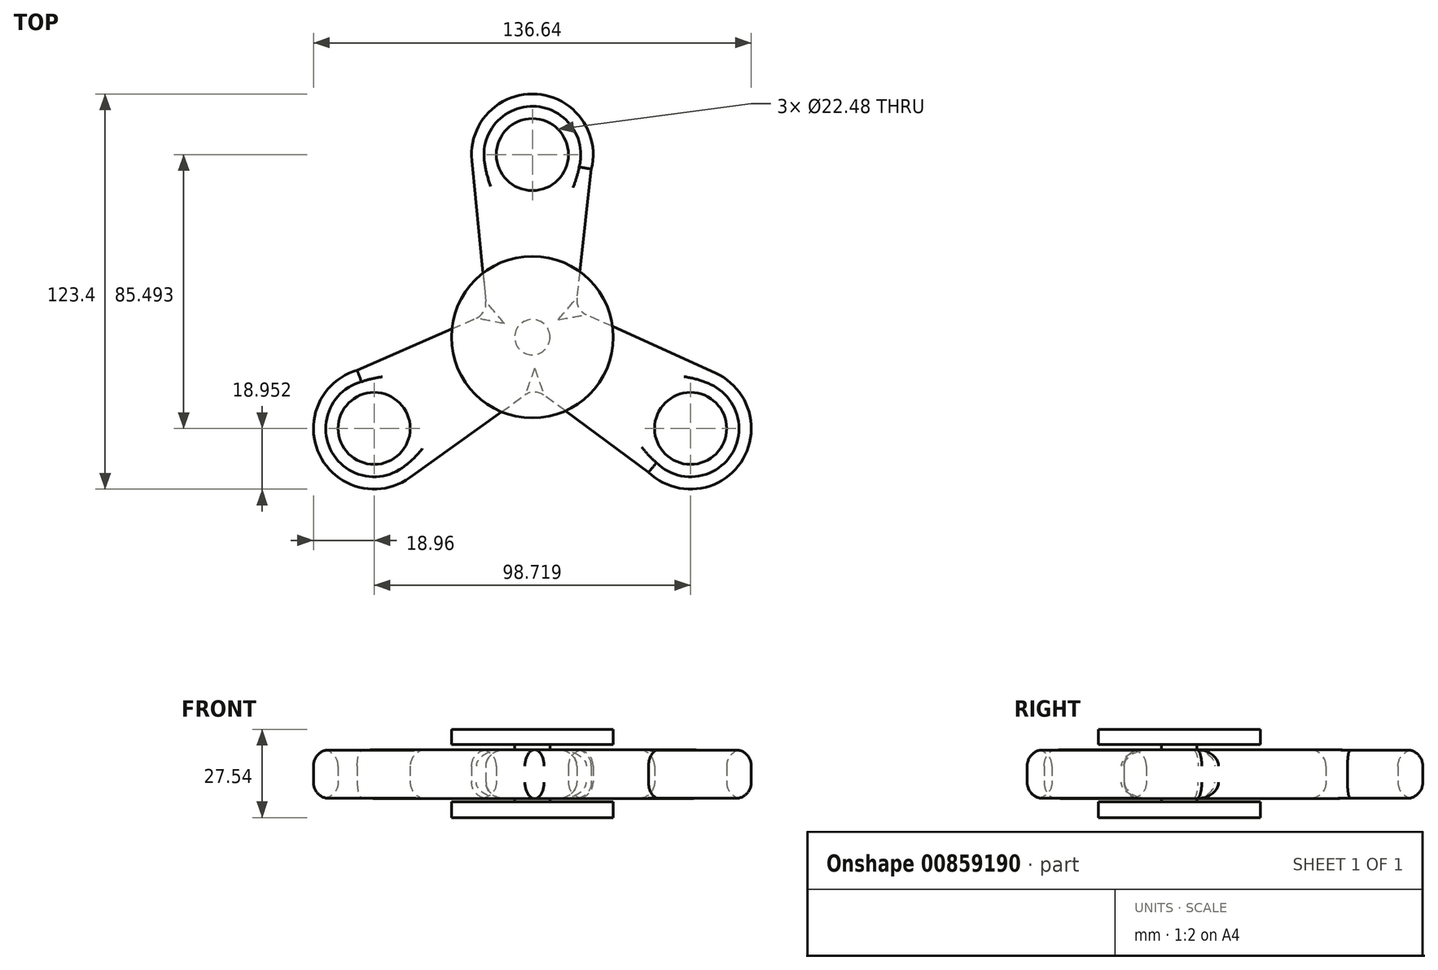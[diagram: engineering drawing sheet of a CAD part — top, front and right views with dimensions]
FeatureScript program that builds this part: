
annotation { "Feature Type Name" : "Feature", "Feature Type Description" : "" }
export const myFeature = defineFeature(function(context is Context, id is Id, definition is map)
    precondition{}
    {
        {
            var Q0;
            Q0=qCreatedBy(makeId("Top.planeOp"),FACE);
            var sketch = newSketch(context, id + "F0", { "sketchPlane" : qUnion([Q0])});
            skArc(sketch, "E0", {"start": v(18.4, 52.47) * mm, "mid": v(1.35, 75.9) * mm, "end": v(-18.86, 55.13) * mm});
            skCircle(sketch, "E1", {"center": v(0, 57) * mm, "radius": 11.24 * mm});
            skLineSegment(sketch, "E2", {"start": v(-18.86, 55.13) * mm, "end": v(-13.4, 0) * mm});
            skLineSegment(sketch, "E3", {"start": v(18.95, 57.32) * mm, "end": v(12.51, 0) * mm});
            skLineSegment(sketch, "E4", {"start": v(12.51, 0) * mm, "end": v(-13.4, 0) * mm});
            skSolve(sketch);
        }
        {
            var Q0;
            Q0 = qSketchRegion(id + "F0", true);
            extrude(context, id + "F1", {"entities" : qUnion([Q0]), "endBound" : BoundingType.SYMMETRIC, "depth" : 15.24 * mm, "offsetDistance" : 25.4 * mm});
        }
        {
            var Q0;
            Q0=qCreatedBy(makeId("Top.planeOp"),FACE);
            var sketch = newSketch(context, id + "F2", { "sketchPlane" : qUnion([Q0])});
            skCircle(sketch, "E5", {"center": v(0, 0) * mm, "radius": 28.62 * mm});
            skSolve(sketch);
        }
        {
            var Q0;
            Q0=makeQuery(id+"F1.opExtrude","SWEPT_BODY",BODY,{"disambiguationData":[OSD([sQuery(id+"F0.wireOp",EDGE,"E0"),sQuery(id+"F0.wireOp",EDGE,"E1"),sQuery(id+"F0.wireOp",EDGE,"E2"),sQuery(id+"F0.wireOp",EDGE,"E3"),sQuery(id+"F0.wireOp",EDGE,"E4")])]});
            var Q1;
            Q1=sQuery(id+"F2.wireOp",EDGE,"E5");
            circularPattern(context, id + "F3", {"operationType" : NewBodyOperationType.ADD, "entities" : qUnion([Q0]), "axis" : qUnion([Q1]), "angle" : 360 * degree, "instanceCount" : 3, "equalSpace" : true});
        }
        {
            var Q0;
            {var subQ0=makeQuery(id+"F1.opExtrude","CAP_FACE",FACE,{"disambiguationData":[OSD([sQuery(id+"F0.wireOp",EDGE,"E0"),sQuery(id+"F0.wireOp",EDGE,"E1"),sQuery(id+"F0.wireOp",EDGE,"E2"),sQuery(id+"F0.wireOp",EDGE,"E3"),sQuery(id+"F0.wireOp",EDGE,"E4")])],"isStart":false});Q0=makeQuery(id+"F3.boolean.opBoolean","MERGE",FACE,{"derivedFrom":[subQ0,makeQuery(id+"F3.opPattern","COPY",FACE,{"derivedFrom":subQ0,"instanceName":"1"}),makeQuery(id+"F3.opPattern","COPY",FACE,{"derivedFrom":subQ0,"instanceName":"2"})]});}
            var Q1;
            Q1=makeQuery(id+"F3.opPattern","COPY",EDGE,{"derivedFrom":makeQuery(id+"F1.opExtrude","CAP_EDGE",EDGE,{"disambiguationData":[OSD([sQuery(id+"F0.wireOp",EDGE,"E3")])],"isStart":true}),"instanceName":"1"});
            var Q2;
            {var subQ0=makeQuery(id+"F1.opExtrude","CAP_FACE",FACE,{"disambiguationData":[OSD([sQuery(id+"F0.wireOp",EDGE,"E0"),sQuery(id+"F0.wireOp",EDGE,"E1"),sQuery(id+"F0.wireOp",EDGE,"E2"),sQuery(id+"F0.wireOp",EDGE,"E3"),sQuery(id+"F0.wireOp",EDGE,"E4")])],"isStart":true});Q2=makeQuery(id+"F3.boolean.opBoolean","MERGE",FACE,{"derivedFrom":[subQ0,makeQuery(id+"F3.opPattern","COPY",FACE,{"derivedFrom":subQ0,"instanceName":"1"}),makeQuery(id+"F3.opPattern","COPY",FACE,{"derivedFrom":subQ0,"instanceName":"2"})]});}
            fillet(context, id + "F4", {"entities" : qUnion([Q0, Q1, Q2]), "radius" : 5.08 * mm, "tangentPropagation" : true, "allowEdgeOverflow" : false});
        }
        {
            var Q0;
            Q0=makeQuery(id+"F3.boolean.opBoolean","INTERSECT",EDGE,{"derivedFrom":[makeQuery(id+"F1.opExtrude","SWEPT_FACE",FACE,{"disambiguationData":[OSD([sQuery(id+"F0.wireOp",EDGE,"E2")])]}),makeQuery(id+"F3.opPattern","COPY",FACE,{"derivedFrom":makeQuery(id+"F1.opExtrude","SWEPT_FACE",FACE,{"disambiguationData":[OSD([sQuery(id+"F0.wireOp",EDGE,"E3")])]}),"instanceName":"1"})]});
            var Q1;
            Q1=makeQuery(id+"F3.boolean.opBoolean","INTERSECT",EDGE,{"derivedFrom":[makeQuery(id+"F1.opExtrude","SWEPT_FACE",FACE,{"disambiguationData":[OSD([sQuery(id+"F0.wireOp",EDGE,"E3")])]}),makeQuery(id+"F3.opPattern","COPY",FACE,{"derivedFrom":makeQuery(id+"F1.opExtrude","SWEPT_FACE",FACE,{"disambiguationData":[OSD([sQuery(id+"F0.wireOp",EDGE,"E2")])]}),"instanceName":"2"})]});
            var Q2;
            Q2=makeQuery(id+"F3.boolean.opBoolean","INTERSECT",EDGE,{"derivedFrom":[makeQuery(id+"F3.opPattern","COPY",FACE,{"derivedFrom":makeQuery(id+"F1.opExtrude","SWEPT_FACE",FACE,{"disambiguationData":[OSD([sQuery(id+"F0.wireOp",EDGE,"E2")])]}),"instanceName":"1"}),makeQuery(id+"F3.opPattern","COPY",FACE,{"derivedFrom":makeQuery(id+"F1.opExtrude","SWEPT_FACE",FACE,{"disambiguationData":[OSD([sQuery(id+"F0.wireOp",EDGE,"E3")])]}),"instanceName":"2"})]});
            fillet(context, id + "F5", {"entities" : qUnion([Q0, Q1, Q2]), "radius" : 5.08 * mm, "tangentPropagation" : true, "allowEdgeOverflow" : false});
        }
        {
            var Q0;
            Q0=qCreatedBy(makeId("Top.planeOp"),FACE);
            var sketch = newSketch(context, id + "F6", { "sketchPlane" : qUnion([Q0])});
            skCircle(sketch, "E6", {"center": v(0, 0) * mm, "radius": 5.51 * mm});
            skSolve(sketch);
        }
        {
            var Q0;
            Q0 = qSketchRegion(id + "F6", true);
            extrude(context, id + "F7", {"entities" : qUnion([Q0]), "operationType" : NewBodyOperationType.ADD, "endBound" : BoundingType.SYMMETRIC, "depth" : 19.3 * mm, "offsetDistance" : 25.4 * mm});
        }
        {
            var Q0;
            Q0=qCreatedBy(makeId("Front.planeOp"),FACE);
            var sketch = newSketch(context, id + "F8", { "sketchPlane" : qUnion([Q0])});
            skLineSegment(sketch, "E7.bottom", {"start": v(0, 14) * mm, "end": v(-25.25, 14) * mm});
            skLineSegment(sketch, "E7.top", {"start": v(0, 9.28) * mm, "end": v(-25.25, 9.28) * mm});
            skLineSegment(sketch, "E7.left", {"start": v(0, 14) * mm, "end": v(0, 9.28) * mm});
            skLineSegment(sketch, "E7.right", {"start": v(-25.25, 14) * mm, "end": v(-25.25, 9.28) * mm});
            skLineSegment(sketch, "E8.bottom", {"start": v(0, -8.66) * mm, "end": v(-25.25, -8.66) * mm});
            skLineSegment(sketch, "E8.top", {"start": v(0, -13.55) * mm, "end": v(-25.25, -13.55) * mm});
            skLineSegment(sketch, "E8.left", {"start": v(0, -8.66) * mm, "end": v(0, -13.55) * mm});
            skLineSegment(sketch, "E8.right", {"start": v(-25.25, -8.66) * mm, "end": v(-25.25, -13.55) * mm});
            skSolve(sketch);
        }
        {
            var Q0;
            Q0 = qSketchRegion(id + "F8", true);
            var Q1;
            Q1=sQuery(id+"F8.wireOp",EDGE,"E8.left");
            revolve(context, id + "F9", {"operationType" : NewBodyOperationType.ADD, "surfaceOperationType" : NewSurfaceOperationType.NEW, "entities" : qUnion([Q0]), "axis" : qUnion([Q1]), "revolveType" : RevolveType.FULL});
        }
    });
